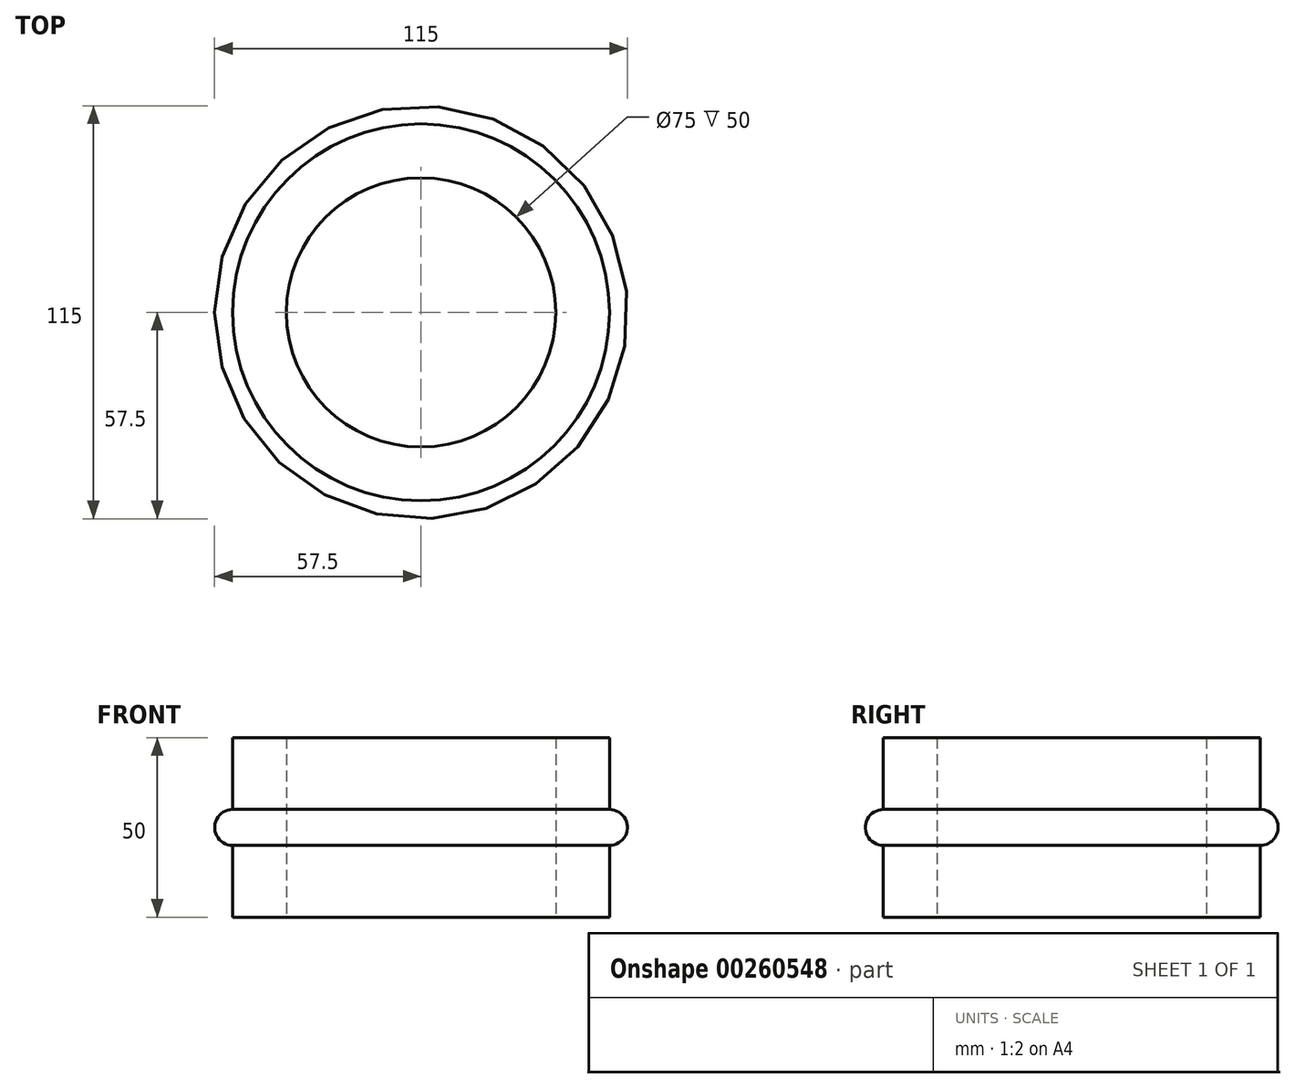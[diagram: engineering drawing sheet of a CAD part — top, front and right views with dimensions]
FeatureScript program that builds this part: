
annotation { "Feature Type Name" : "Feature", "Feature Type Description" : "" }
export const myFeature = defineFeature(function(context is Context, id is Id, definition is map)
    precondition{}
    {
        {
            var Q0;
            Q0=qCreatedBy(makeId("Front.planeOp"),FACE);
            var sketch = newSketch(context, id + "F0", { "sketchPlane" : qUnion([Q0])});
            skLineSegment(sketch, "E0", {"start": v(0, 0) * mm, "end": v(0, 50) * mm, "construction": true});
            skLineSegment(sketch, "E1.bottom", {"start": v(37.5, 0) * mm, "end": v(52.5, 0) * mm});
            skLineSegment(sketch, "E1.top", {"start": v(37.5, 50) * mm, "end": v(52.5, 50) * mm});
            skLineSegment(sketch, "E1.left", {"start": v(37.5, 0) * mm, "end": v(37.5, 50) * mm});
            skLineSegment(sketch, "E1.right", {"start": v(52.5, 0) * mm, "end": v(52.5, 50) * mm});
            skCircle(sketch, "E2", {"center": v(52.5, 25) * mm, "radius": 5 * mm});
            skSolve(sketch);
        }
        {
            var Q0;
            {var subQ1=sQuery(id+"F0.wireOp",EDGE,"E1.bottom");Q0=makeQuery(id+"F0.imprint","IMPRINT",FACE,{"disambiguationData":[TD([[makeQuery(id+"F0.imprint","IMPRINT",EDGE,{"derivedFrom":subQ1}),1.0]])]});}
            var Q1;
            {var subQ0=sQuery(id+"F0.wireOp",EDGE,"E2");var subQ1=sQuery(id+"F0.wireOp",EDGE,"E1.right");var subQ2=makeQuery(id+"F0.imprint","INTERSECT",VERTEX,{"disambiguationData":[OD(0.0)],"derivedFrom":[subQ1,subQ0]});Q1=makeQuery(id+"F0.imprint","IMPRINT",FACE,{"disambiguationData":[TD([[makeQuery(id+"F0.imprint","IMPRINT",EDGE,{"disambiguationData":[TD([[subQ2,-1.0]])],"derivedFrom":subQ1}),1.0]])]});}
            var Q2;
            {var subQ0=sQuery(id+"F0.wireOp",EDGE,"E2");var subQ1=sQuery(id+"F0.wireOp",EDGE,"E1.right");var subQ2=makeQuery(id+"F0.imprint","INTERSECT",VERTEX,{"disambiguationData":[OD(0.0)],"derivedFrom":[subQ1,subQ0]});Q2=makeQuery(id+"F0.imprint","IMPRINT",FACE,{"disambiguationData":[TD([[makeQuery(id+"F0.imprint","IMPRINT",EDGE,{"disambiguationData":[TD([[subQ2,-1.0]])],"derivedFrom":subQ1}),-1.0]])]});}
            var Q3;
            Q3=sQuery(id+"F0.wireOp",EDGE,"E0");
            revolve(context, id + "F1", {"entities" : qUnion([Q0, Q1, Q2]), "axis" : qUnion([Q3]), "revolveType" : RevolveType.FULL});
        }
    });
